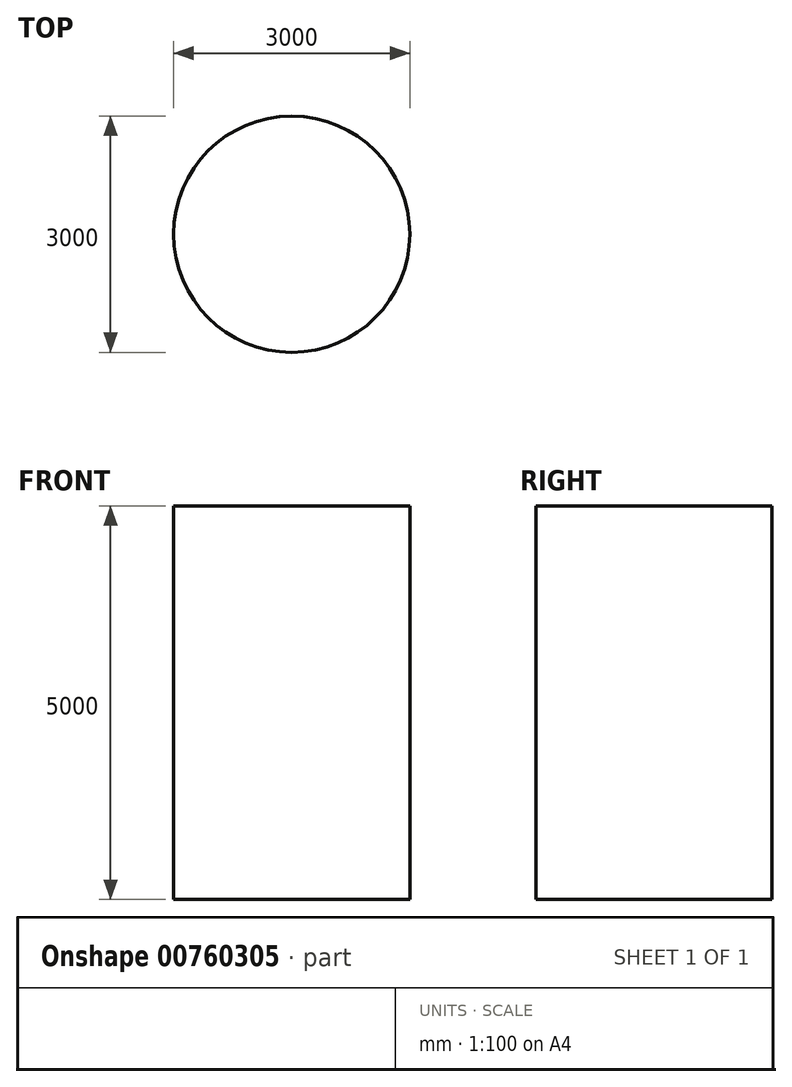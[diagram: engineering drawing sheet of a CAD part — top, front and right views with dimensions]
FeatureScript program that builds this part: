
annotation { "Feature Type Name" : "Feature", "Feature Type Description" : "" }
export const myFeature = defineFeature(function(context is Context, id is Id, definition is map)
    precondition{}
    {
        {
            var Q0;
            Q0=qCreatedBy(makeId("Top.planeOp"),FACE);
            var sketch = newSketch(context, id + "F0", { "sketchPlane" : qUnion([Q0])});
            skCircle(sketch, "E0", {"center": v(0, 0) * mm, "radius": 1500 * mm});
            skSolve(sketch);
        }
        {
            var Q0;
            Q0 = qSketchRegion(id + "F0", true);
            extrude(context, id + "F1", {"entities" : qUnion([Q0]), "depth" : 5000 * mm, "offsetDistance" : 25 * mm});
        }
    });
